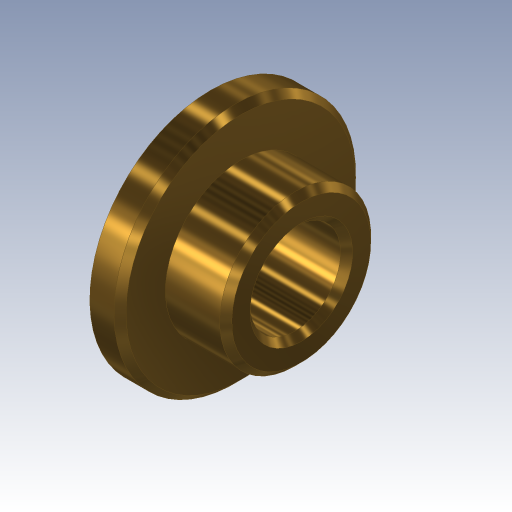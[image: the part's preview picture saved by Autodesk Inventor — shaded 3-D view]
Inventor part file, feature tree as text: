
AUTODESK INVENTOR PART (.ipt)
format: ipt  version: 2023.3 (Build 273359000, 359)  size: 210,432 bytes
history: native  units: in
note: dims shown in document units (in); Inventor stores cm internally (conversion verified against a paired STEP export)
features: revolve x1, chamfer x1, sketch x1
ambient origin geometry x8: Origin, YZ Plane, XZ Plane, XY Plane, X Axis, Y Axis, Z Axis, Center Point
bodies: Body1 (feature_tree)
feature tree (3):
  revolve  "Umdrehung1"
  chamfer  "Fase1"  Distance=0.1181in
  sketch  "Skizze3"  dims[d4=0.0394in d5=0.1181in d6=0.1181in d7=0.315in d8=0.1969in d9=90.0deg d10=0.0079in d11=0.0787in d12=45.0deg]
